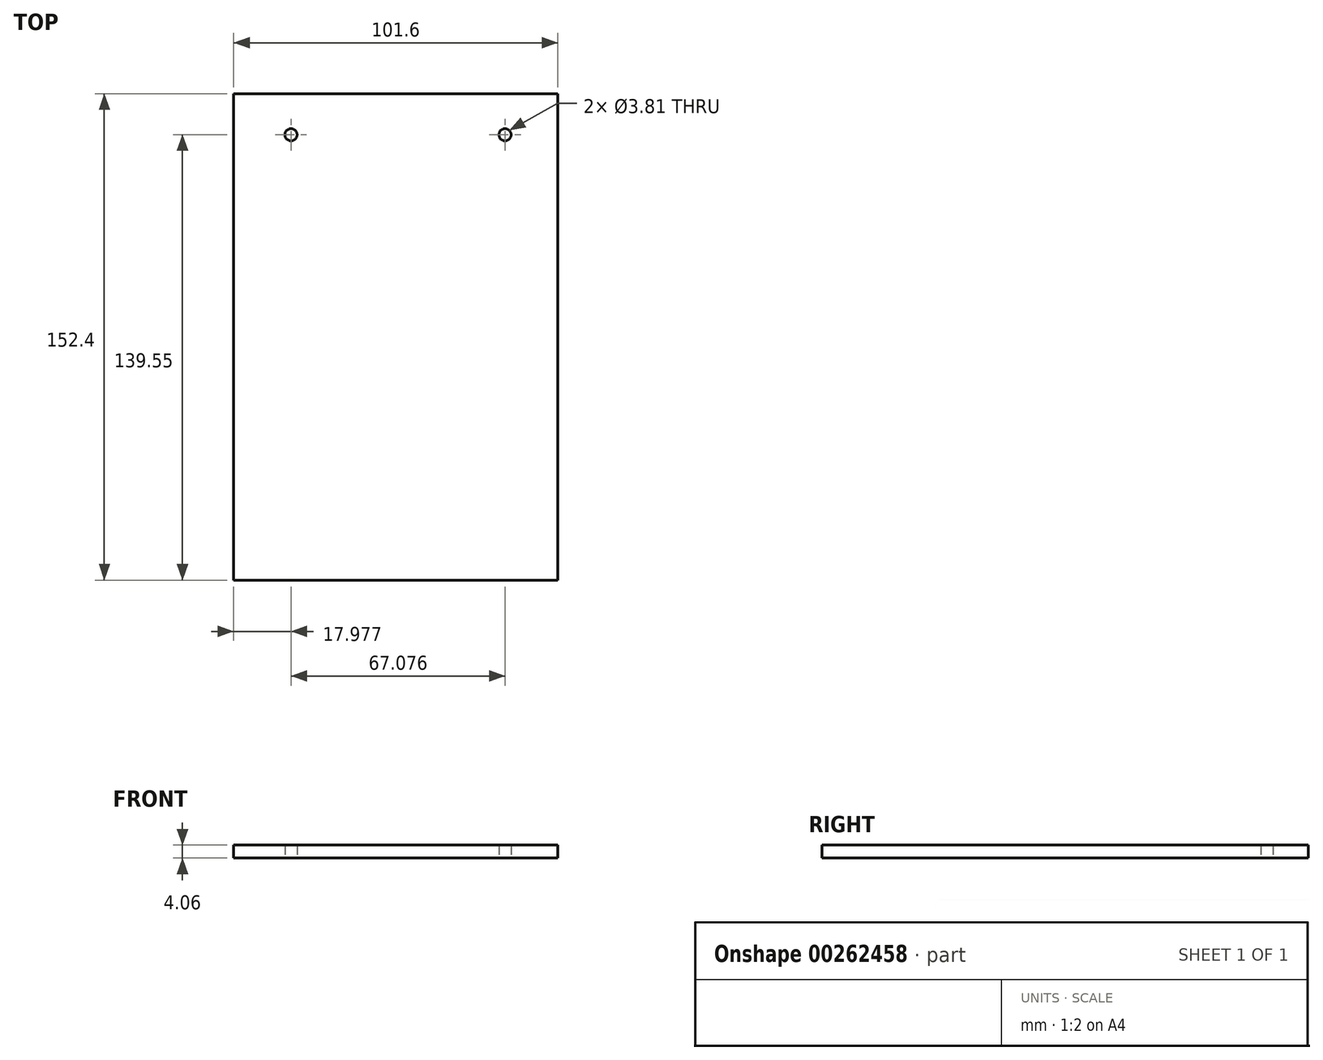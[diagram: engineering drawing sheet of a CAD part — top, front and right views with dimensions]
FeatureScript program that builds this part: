
annotation { "Feature Type Name" : "Feature", "Feature Type Description" : "" }
export const myFeature = defineFeature(function(context is Context, id is Id, definition is map)
    precondition{}
    {
        {
            var Q0;
            Q0=qCreatedBy(makeId("Top.planeOp"),FACE);
            var sketch = newSketch(context, id + "F0", { "sketchPlane" : qUnion([Q0])});
            skLineSegment(sketch, "E0.bottom", {"start": v(28.95, 87.96) * mm, "end": v(-72.65, 87.96) * mm});
            skLineSegment(sketch, "E0.top", {"start": v(28.95, -64.44) * mm, "end": v(-72.65, -64.44) * mm});
            skLineSegment(sketch, "E0.left", {"start": v(28.95, 87.96) * mm, "end": v(28.95, -64.44) * mm});
            skLineSegment(sketch, "E0.right", {"start": v(-72.65, 87.96) * mm, "end": v(-72.65, -64.44) * mm});
            skSolve(sketch);
        }
        {
            var Q0;
            Q0=makeQuery(id+"F0.imprint","IMPRINT",FACE,{"disambiguationData":[TD([[makeQuery(id+"F0.imprint","IMPRINT",EDGE,{"derivedFrom":sQuery(id+"F0.wireOp",EDGE,"E0.bottom")}),1.0]])]});
            extrude(context, id + "F1", {"entities" : qUnion([Q0]), "depth" : 4.06 * mm});
        }
        {
            var Q0;
            Q0=qCreatedBy(makeId("Top.planeOp"),FACE);
            var sketch = newSketch(context, id + "F2", { "sketchPlane" : qUnion([Q0])});
            skLineSegment(sketch, "E1.bottom", {"start": v(-54.67, 60.18) * mm, "end": v(12.4, 60.18) * mm});
            skLineSegment(sketch, "E1.top", {"start": v(-54.67, 75.11) * mm, "end": v(12.4, 75.11) * mm});
            skLineSegment(sketch, "E1.left", {"start": v(-54.67, 60.18) * mm, "end": v(-54.67, 75.11) * mm});
            skLineSegment(sketch, "E1.right", {"start": v(12.4, 60.18) * mm, "end": v(12.4, 75.11) * mm});
            skSolve(sketch);
        }
        {
            var Q0;
            Q0=sQuery(id+"F2.wireOp",VERTEX,"E1.top.end");
            var Q1;
            Q1=sQuery(id+"F2.wireOp",VERTEX,"E1.left.end");
            var Q2;
            Q2=makeQuery(id+"F1.opExtrude","SWEPT_BODY",BODY,{"disambiguationData":[OSD([sQuery(id+"F0.wireOp",EDGE,"E0.bottom"),sQuery(id+"F0.wireOp",EDGE,"E0.top"),sQuery(id+"F0.wireOp",EDGE,"E0.left"),sQuery(id+"F0.wireOp",EDGE,"E0.right")])]});
            hole(context, id + "F3", {"style" : HoleStyle.C_BORE, "endStyle" : HoleEndStyle.THROUGH, "oppositeDirection" : true, "holeDiameter" : 3.8 * mm, "cBoreDiameter" : 3.8 * mm, "cBoreDepth" : 0.25 * mm, "tappedDepth" : 12.7 * mm, "tapClearance" : 3, "startFromSketch" : true, "locations" : qUnion([Q0, Q1]), "scope" : qUnion([Q2])});
        }
    });
